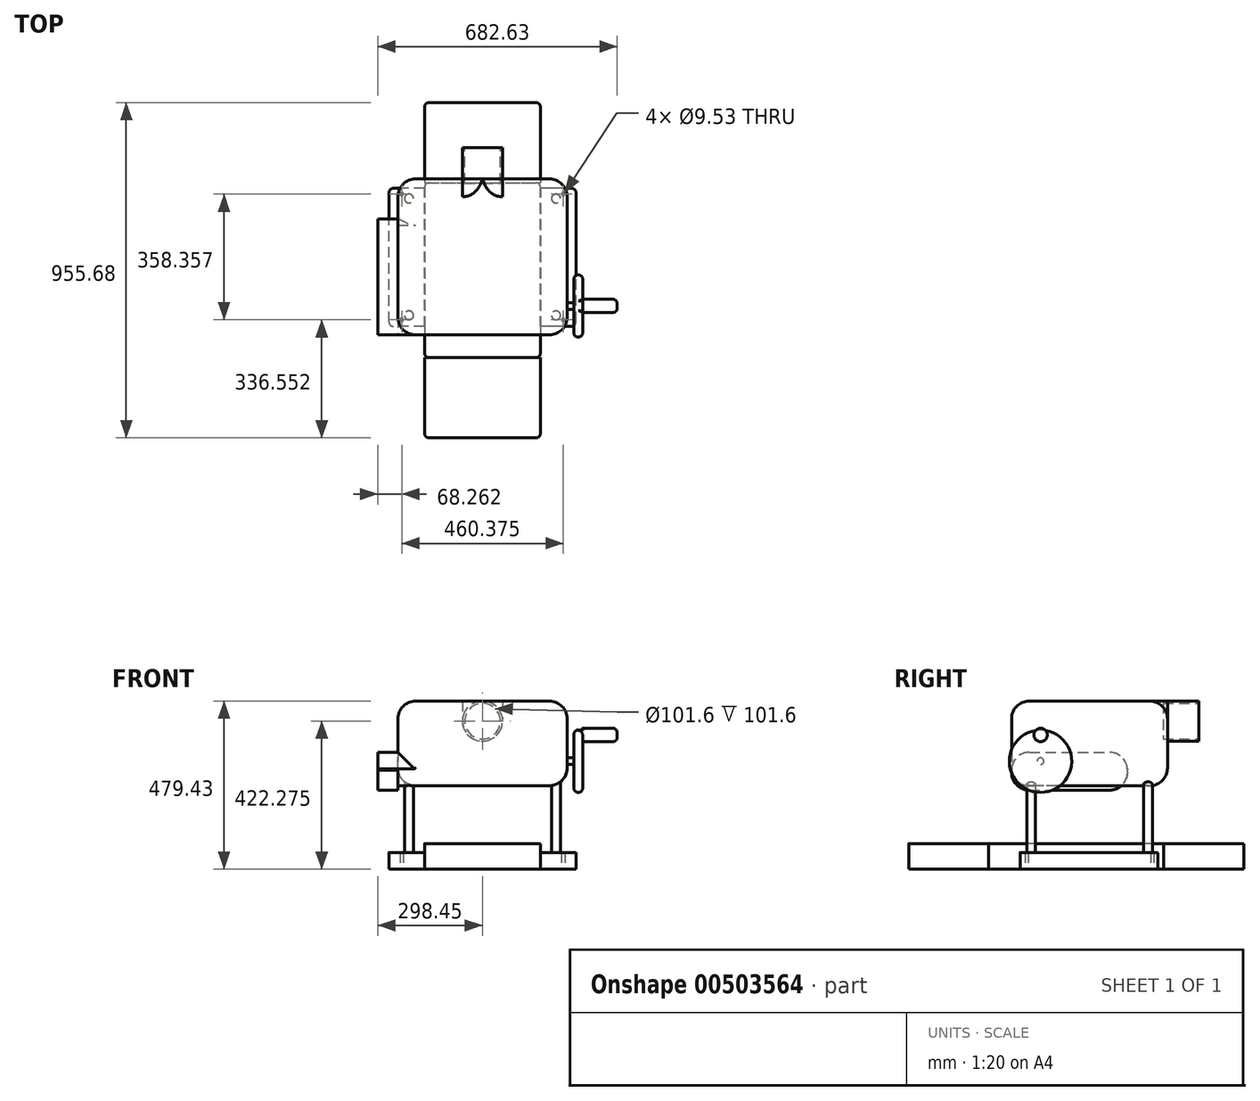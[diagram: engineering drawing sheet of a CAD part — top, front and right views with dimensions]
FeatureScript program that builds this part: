
annotation { "Feature Type Name" : "Feature", "Feature Type Description" : "" }
export const myFeature = defineFeature(function(context is Context, id is Id, definition is map)
    precondition{}
    {
        {
            var Q0;
            Q0=qCreatedBy(makeId("Top.planeOp"),FACE);
            var sketch = newSketch(context, id + "F0", { "sketchPlane" : qUnion([Q0])});
            skLineSegment(sketch, "E0.bottom", {"start": v(266.7, -198.23) * mm, "end": v(-266.7, -198.23) * mm});
            skLineSegment(sketch, "E0.top", {"start": v(266.7, 195.47) * mm, "end": v(-266.7, 195.47) * mm});
            skLineSegment(sketch, "E0.left", {"start": v(266.7, -198.23) * mm, "end": v(266.7, 195.47) * mm});
            skLineSegment(sketch, "E0.right", {"start": v(-266.7, -198.23) * mm, "end": v(-266.7, 195.47) * mm});
            skLineSegment(sketch, "E1", {"start": v(0, 195.47) * mm, "end": v(0, -198.23) * mm, "construction": true});
            skCircle(sketch, "E2", {"center": v(230.19, -179.18) * mm, "radius": 4.76 * mm});
            skCircle(sketch, "E3.MirrorC", {"center": v(-230.19, -179.18) * mm, "radius": 4.76 * mm});
            skCircle(sketch, "E4.MirrorC", {"center": v(230.19, 179.18) * mm, "radius": 4.76 * mm});
            skCircle(sketch, "E5.MirrorC", {"center": v(-230.19, 179.18) * mm, "radius": 4.76 * mm});
            skSolve(sketch);
        }
        {
            var Q0;
            Q0 = qSketchRegion(id + "F0", true);
            extrude(context, id + "F1", {"entities" : qUnion([Q0]), "depth" : 47.62 * mm});
        }
        {
            var Q0;
            Q0=makeQuery(id+"F4.boolean.opBoolean","MERGE",FACE,{"derivedFrom":[makeQuery(id+"F1.opExtrude","SWEPT_FACE",FACE,{"disambiguationData":[OSD([sQuery(id+"F0.wireOp",EDGE,"E0.bottom")])]}),makeQuery(id+"F4.opExtrude","CAP_FACE",FACE,{"disambiguationData":[OSD([sQuery(id+"F3.wireOp",EDGE,"E6.bottom"),sQuery(id+"F3.wireOp",EDGE,"E6.top"),sQuery(id+"F3.wireOp",EDGE,"E6.left"),sQuery(id+"F3.wireOp",EDGE,"E6.right")])],"isStart":true})]});
            cPlane(context, id + "F2", {"entities" : qUnion([Q0]), "cplaneType" : CPlaneType.OFFSET, "offset" : 88.9 * mm, "width" : 152.4 * mm, "height" : 152.4 * mm});
        }
        {
            var Q0;
            Q0=qCreatedBy(id+"F2.planeOp",FACE);
            var sketch = newSketch(context, id + "F3", { "sketchPlane" : qUnion([Q0])});
            skLineSegment(sketch, "E6.bottom", {"start": v(-165.1, 0) * mm, "end": v(165.1, 0) * mm});
            skLineSegment(sketch, "E6.top", {"start": v(-165.1, 73.03) * mm, "end": v(165.1, 73.03) * mm});
            skLineSegment(sketch, "E6.left", {"start": v(-165.1, 0) * mm, "end": v(-165.1, 73.03) * mm});
            skLineSegment(sketch, "E6.right", {"start": v(165.1, 0) * mm, "end": v(165.1, 73.03) * mm});
            skLineSegment(sketch, "E7", {"start": v(0, 73.03) * mm, "end": v(0, 0) * mm, "construction": true});
            skSolve(sketch);
        }
        {
            var Q0;
            Q0 = qSketchRegion(id + "F3", true);
            extrude(context, id + "F4", {"entities" : qUnion([Q0]), "operationType" : NewBodyOperationType.ADD, "oppositeDirection" : true, "depth" : 498.47 * mm});
        }
        {
            var Q0;
            {var subQ0=sQuery(id+"F0.wireOp",EDGE,"E3.MirrorC");var subQ1=sQuery(id+"F0.wireOp",EDGE,"E0.top");var subQ2=sQuery(id+"F0.wireOp",EDGE,"E0.right");var subQ3=sQuery(id+"F0.wireOp",EDGE,"E0.bottom");var subQ4=sQuery(id+"F0.wireOp",EDGE,"E5.MirrorC");Q0=makeQuery(id+"F4.boolean.opBoolean","SPLIT",FACE,{"disambiguationData":[TD([makeQuery(id+"F1.opExtrude","SWEPT_FACE",FACE,{"disambiguationData":[OSD([subQ2])]})])],"derivedFrom":makeQuery(id+"F1.opExtrude","CAP_FACE",FACE,{"disambiguationData":[OSD([subQ3,subQ1,sQuery(id+"F0.wireOp",EDGE,"E0.left"),subQ2,sQuery(id+"F0.wireOp",EDGE,"E2"),subQ0,sQuery(id+"F0.wireOp",EDGE,"E4.MirrorC"),subQ4])],"isStart":false})});}
            var sketch = newSketch(context, id + "F5", { "sketchPlane" : qUnion([Q0])});
            skCircle(sketch, "E8", {"center": v(-209.55, -166.48) * mm, "radius": 12.7 * mm});
            skCircle(sketch, "E9.MirrorC", {"center": v(-209.55, 166.48) * mm, "radius": 12.7 * mm});
            skCircle(sketch, "E10.MirrorC", {"center": v(209.55, 166.48) * mm, "radius": 12.7 * mm});
            skCircle(sketch, "E11.MirrorC", {"center": v(209.55, -166.48) * mm, "radius": 12.7 * mm});
            skSolve(sketch);
        }
        {
            var Q0;
            Q0 = qSketchRegion(id + "F5", true);
            extrude(context, id + "F6", {"entities" : qUnion([Q0]), "operationType" : NewBodyOperationType.ADD, "depth" : 190.5 * mm});
        }
        {
            var Q0;
            Q0=makeQuery(id+"F6.opExtrude","CAP_FACE",FACE,{"disambiguationData":[OSD([sQuery(id+"F5.wireOp",EDGE,"E8")])],"isStart":false});
            var sketch = newSketch(context, id + "F7", { "sketchPlane" : qUnion([Q0])});
            skLineSegment(sketch, "E12.bottom", {"start": v(-241.3, 222.25) * mm, "end": v(241.3, 222.25) * mm});
            skLineSegment(sketch, "E12.top", {"start": v(-241.3, -222.25) * mm, "end": v(241.3, -222.25) * mm});
            skLineSegment(sketch, "E12.left", {"start": v(-241.3, 222.25) * mm, "end": v(-241.3, -222.25) * mm});
            skLineSegment(sketch, "E12.right", {"start": v(241.3, 222.25) * mm, "end": v(241.3, -222.25) * mm});
            skPoint(sketch, "E12.middle", {"position": v(0, 0) * mm});
            skSolve(sketch);
        }
        {
            var Q0;
            Q0 = qSketchRegion(id + "F7", true);
            extrude(context, id + "F8", {"entities" : qUnion([Q0]), "operationType" : NewBodyOperationType.ADD, "depth" : 241.3 * mm});
        }
        {
            var Q0;
            Q0=makeQuery(id+"F8.opExtrude","SWEPT_FACE",FACE,{"disambiguationData":[OSD([sQuery(id+"F7.wireOp",EDGE,"E12.right")])]});
            var sketch = newSketch(context, id + "F9", { "sketchPlane" : qUnion([Q0])});
            skCircle(sketch, "E13", {"center": v(-139.7, 307.98) * mm, "radius": 9.52 * mm});
            skSolve(sketch);
        }
        {
            var Q0;
            Q0 = qSketchRegion(id + "F9", true);
            extrude(context, id + "F10", {"entities" : qUnion([Q0]), "operationType" : NewBodyOperationType.ADD, "depth" : 19.05 * mm});
        }
        {
            var Q0;
            Q0=makeQuery(id+"F10.opExtrude","CAP_FACE",FACE,{"disambiguationData":[OSD([sQuery(id+"F9.wireOp",EDGE,"E13")])],"isStart":false});
            var sketch = newSketch(context, id + "F11", { "sketchPlane" : qUnion([Q0])});
            skCircle(sketch, "E14", {"center": v(-139.7, 307.98) * mm, "radius": 88.9 * mm});
            skSolve(sketch);
        }
        {
            var Q0;
            Q0 = qSketchRegion(id + "F11", true);
            extrude(context, id + "F12", {"entities" : qUnion([Q0]), "operationType" : NewBodyOperationType.ADD, "depth" : 25.4 * mm});
        }
        {
            var Q0;
            Q0=makeQuery(id+"F12.opExtrude","CAP_FACE",FACE,{"disambiguationData":[OSD([sQuery(id+"F11.wireOp",EDGE,"E14")])],"isStart":false});
            var sketch = newSketch(context, id + "F13", { "sketchPlane" : qUnion([Q0])});
            skCircle(sketch, "E15", {"center": v(-139.45, 382.88) * mm, "radius": 19.05 * mm});
            skSolve(sketch);
        }
        {
            var Q0;
            Q0 = qSketchRegion(id + "F13", true);
            extrude(context, id + "F14", {"entities" : qUnion([Q0]), "operationType" : NewBodyOperationType.ADD, "depth" : 98.42 * mm});
        }
        {
            var Q0;
            Q0=makeQuery(id+"F4.opExtrude","CAP_FACE",FACE,{"disambiguationData":[OSD([sQuery(id+"F3.wireOp",EDGE,"E6.bottom"),sQuery(id+"F3.wireOp",EDGE,"E6.top"),sQuery(id+"F3.wireOp",EDGE,"E6.left"),sQuery(id+"F3.wireOp",EDGE,"E6.right")])],"isStart":true});
            var sketch = newSketch(context, id + "F15", { "sketchPlane" : qUnion([Q0])});
            skLineSegment(sketch, "E16.0.0", {"start": v(165.1, 73.03) * mm, "end": v(-165.1, 73.03) * mm});
            skLineSegment(sketch, "E16.0.1", {"start": v(-165.1, 73.03) * mm, "end": v(-165.1, 0) * mm});
            skLineSegment(sketch, "E16.0.2", {"start": v(-165.1, 0) * mm, "end": v(165.1, 0) * mm});
            skLineSegment(sketch, "E16.0.3", {"start": v(165.1, 0) * mm, "end": v(165.1, 73.03) * mm});
            skSolve(sketch);
        }
        {
            var Q0;
            Q0 = qSketchRegion(id + "F15", true);
            extrude(context, id + "F16", {"entities" : qUnion([Q0]), "depth" : 228.6 * mm});
        }
        {
            var Q0;
            Q0=makeQuery(id+"F4.opExtrude","CAP_FACE",FACE,{"disambiguationData":[OSD([sQuery(id+"F3.wireOp",EDGE,"E6.bottom"),sQuery(id+"F3.wireOp",EDGE,"E6.top"),sQuery(id+"F3.wireOp",EDGE,"E6.left"),sQuery(id+"F3.wireOp",EDGE,"E6.right")])],"isStart":false});
            var sketch = newSketch(context, id + "F17", { "sketchPlane" : qUnion([Q0])});
            skLineSegment(sketch, "E17.0.0", {"start": v(165.1, 73.03) * mm, "end": v(-165.1, 73.03) * mm});
            skLineSegment(sketch, "E17.0.1", {"start": v(-165.1, 73.03) * mm, "end": v(-165.1, 0) * mm});
            skLineSegment(sketch, "E17.0.2", {"start": v(-165.1, 0) * mm, "end": v(165.1, 0) * mm});
            skLineSegment(sketch, "E17.0.3", {"start": v(165.1, 0) * mm, "end": v(165.1, 73.03) * mm});
            skSolve(sketch);
        }
        {
            var Q0;
            Q0 = qSketchRegion(id + "F17", true);
            extrude(context, id + "F18", {"entities" : qUnion([Q0]), "depth" : 228.6 * mm});
        }
        {
            var Q0;
            Q0=makeQuery(id+"F8.opExtrude","SWEPT_FACE",FACE,{"disambiguationData":[OSD([sQuery(id+"F7.wireOp",EDGE,"E12.left")])]});
            var sketch = newSketch(context, id + "F19", { "sketchPlane" : qUnion([Q0])});
            skLineSegment(sketch, "E18.bottom", {"start": v(222.25, 225.43) * mm, "end": v(-107.95, 225.43) * mm});
            skLineSegment(sketch, "E18.top", {"start": v(222.25, 333.38) * mm, "end": v(-107.95, 333.38) * mm});
            skLineSegment(sketch, "E18.left", {"start": v(222.25, 225.43) * mm, "end": v(222.25, 333.38) * mm});
            skLineSegment(sketch, "E18.right", {"start": v(-107.95, 225.43) * mm, "end": v(-107.95, 333.38) * mm});
            skPoint(sketch, "E18.middle", {"position": v(57.15, 279.4) * mm});
            skSolve(sketch);
        }
        {
            var Q0;
            Q0 = qSketchRegion(id + "F19", true);
            extrude(context, id + "F20", {"entities" : qUnion([Q0]), "operationType" : NewBodyOperationType.ADD, "depth" : 57.15 * mm});
        }
        {
            var Q0;
            Q0=makeQuery(id+"F8.opExtrude","SWEPT_FACE",FACE,{"disambiguationData":[OSD([sQuery(id+"F7.wireOp",EDGE,"E12.bottom")])]});
            var sketch = newSketch(context, id + "F21", { "sketchPlane" : qUnion([Q0])});
            skCircle(sketch, "E19", {"center": v(0, 422.28) * mm, "radius": 57.15 * mm});
            skSolve(sketch);
        }
        {
            var Q0;
            Q0 = qSketchRegion(id + "F21", true);
            extrude(context, id + "F22", {"entities" : qUnion([Q0]), "operationType" : NewBodyOperationType.ADD, "depth" : 88.9 * mm});
        }
        {
            var Q0;
            Q0=makeQuery(id+"F8.opExtrude","SWEPT_EDGE",EDGE,{"disambiguationData":[OSD([sQuery(id+"F7.wireOp",EDGE,"E12.top"),sQuery(id+"F7.wireOp",EDGE,"E12.right")])]});
            var Q1;
            Q1=makeQuery(id+"F8.opExtrude","SWEPT_EDGE",EDGE,{"disambiguationData":[OSD([sQuery(id+"F7.wireOp",EDGE,"E12.top"),sQuery(id+"F7.wireOp",EDGE,"E12.left")])]});
            var Q2;
            Q2=makeQuery(id+"F8.opExtrude","SWEPT_EDGE",EDGE,{"disambiguationData":[OSD([sQuery(id+"F7.wireOp",EDGE,"E12.bottom"),sQuery(id+"F7.wireOp",EDGE,"E12.right")])]});
            var Q3;
            Q3=makeQuery(id+"F8.opExtrude","SWEPT_EDGE",EDGE,{"disambiguationData":[OSD([sQuery(id+"F7.wireOp",EDGE,"E12.bottom"),sQuery(id+"F7.wireOp",EDGE,"E12.left")])]});
            var Q4;
            Q4=makeQuery(id+"F8.opExtrude","CAP_FACE",FACE,{"disambiguationData":[OSD([sQuery(id+"F7.wireOp",EDGE,"E12.bottom"),sQuery(id+"F7.wireOp",EDGE,"E12.top"),sQuery(id+"F7.wireOp",EDGE,"E12.left"),sQuery(id+"F7.wireOp",EDGE,"E12.right")])],"isStart":false});
            fillet(context, id + "F23", {"entities" : qUnion([Q0, Q1, Q2, Q3, Q4]), "radius" : 50.8 * mm, "tangentPropagation" : true, "allowEdgeOverflow" : false});
        }
        {
            var Q0;
            Q0=makeQuery(id+"F1.opExtrude","SWEPT_EDGE",EDGE,{"disambiguationData":[OSD([sQuery(id+"F0.wireOp",EDGE,"E0.top"),sQuery(id+"F0.wireOp",EDGE,"E0.left")])]});
            var Q1;
            Q1=makeQuery(id+"F1.opExtrude","SWEPT_EDGE",EDGE,{"disambiguationData":[OSD([sQuery(id+"F0.wireOp",EDGE,"E0.bottom"),sQuery(id+"F0.wireOp",EDGE,"E0.left")])]});
            var Q2;
            Q2=makeQuery(id+"F4.opExtrude","CAP_EDGE",EDGE,{"disambiguationData":[OSD([sQuery(id+"F3.wireOp",EDGE,"E6.right")])],"isStart":true});
            var Q3;
            Q3=makeQuery(id+"F4.opExtrude","CAP_EDGE",EDGE,{"disambiguationData":[OSD([sQuery(id+"F3.wireOp",EDGE,"E6.right")])],"isStart":false});
            var Q4;
            Q4=makeQuery(id+"F1.opExtrude","SWEPT_EDGE",EDGE,{"disambiguationData":[OSD([sQuery(id+"F0.wireOp",EDGE,"E0.top"),sQuery(id+"F0.wireOp",EDGE,"E0.right")])]});
            var Q5;
            Q5=makeQuery(id+"F1.opExtrude","SWEPT_EDGE",EDGE,{"disambiguationData":[OSD([sQuery(id+"F0.wireOp",EDGE,"E0.bottom"),sQuery(id+"F0.wireOp",EDGE,"E0.right")])]});
            var Q6;
            Q6=makeQuery(id+"F4.opExtrude","CAP_EDGE",EDGE,{"disambiguationData":[OSD([sQuery(id+"F3.wireOp",EDGE,"E6.left")])],"isStart":true});
            var Q7;
            Q7=makeQuery(id+"F4.opExtrude","CAP_EDGE",EDGE,{"disambiguationData":[OSD([sQuery(id+"F3.wireOp",EDGE,"E6.left")])],"isStart":false});
            var Q8;
            Q8=makeQuery(id+"F18.opExtrude","CAP_EDGE",EDGE,{"disambiguationData":[OSD([sQuery(id+"F17.wireOp",EDGE,"E17.0.3")])],"isStart":false});
            var Q9;
            Q9=makeQuery(id+"F18.opExtrude","CAP_EDGE",EDGE,{"disambiguationData":[OSD([sQuery(id+"F17.wireOp",EDGE,"E17.0.1")])],"isStart":false});
            var Q10;
            Q10=makeQuery(id+"F16.opExtrude","CAP_EDGE",EDGE,{"disambiguationData":[OSD([sQuery(id+"F15.wireOp",EDGE,"E16.0.1")])],"isStart":false});
            var Q11;
            Q11=makeQuery(id+"F16.opExtrude","CAP_EDGE",EDGE,{"disambiguationData":[OSD([sQuery(id+"F15.wireOp",EDGE,"E16.0.3")])],"isStart":false});
            var Q12;
            {var subQ0=sQuery(id+"F11.wireOp",EDGE,"E14");Q12=makeQuery(id+"F14.boolean.opBoolean","SPLIT",EDGE,{"disambiguationData":[topologyDisambiguationEdgeConnected([makeQuery(id+"F12.opExtrude","CAP_FACE",FACE,{"disambiguationData":[OSD([subQ0])],"isStart":false})])],"derivedFrom":makeQuery(id+"F12.opExtrude","CAP_EDGE",EDGE,{"disambiguationData":[OSD([subQ0])],"isStart":false})});}
            var Q13;
            Q13=makeQuery(id+"F12.opExtrude","CAP_EDGE",EDGE,{"disambiguationData":[OSD([sQuery(id+"F11.wireOp",EDGE,"E14")])],"isStart":true});
            var Q14;
            Q14=makeQuery(id+"F14.opExtrude","CAP_EDGE",EDGE,{"disambiguationData":[OSD([sQuery(id+"F13.wireOp",EDGE,"E15")])],"isStart":false});
            fillet(context, id + "F24", {"entities" : qUnion([Q0, Q1, Q2, Q3, Q4, Q5, Q6, Q7, Q8, Q9, Q10, Q11, Q12, Q13, Q14]), "radius" : 12.7 * mm, "tangentPropagation" : true, "allowEdgeOverflow" : false});
        }
        {
            var Q0;
            Q0=makeQuery(id+"F22.opExtrude","CAP_FACE",FACE,{"disambiguationData":[OSD([sQuery(id+"F21.wireOp",EDGE,"E19")])],"isStart":false});
            var sketch = newSketch(context, id + "F25", { "sketchPlane" : qUnion([Q0])});
            skCircle(sketch, "E20.0", {"center": v(0, 422.28) * mm, "radius": 50.8 * mm});
            skSolve(sketch);
        }
        {
            var Q0;
            Q0 = qSketchRegion(id + "F25", true);
            extrude(context, id + "F26", {"entities" : qUnion([Q0]), "operationType" : NewBodyOperationType.REMOVE, "oppositeDirection" : true, "depth" : 101.6 * mm});
        }
        {
            var Q0;
            Q0=makeQuery(id+"F20.opExtrude","SWEPT_EDGE",EDGE,{"disambiguationData":[OSD([sQuery(id+"F19.wireOp",EDGE,"E18.top"),sQuery(id+"F19.wireOp",EDGE,"E18.right")])]});
            var Q1;
            Q1=makeQuery(id+"F20.opExtrude","SWEPT_EDGE",EDGE,{"disambiguationData":[OSD([sQuery(id+"F19.wireOp",EDGE,"E18.bottom"),sQuery(id+"F19.wireOp",EDGE,"E18.right")])]});
            var Q2;
            Q2=makeQuery(id+"F20.opExtrude","SWEPT_EDGE",EDGE,{"disambiguationData":[OSD([sQuery(id+"F19.wireOp",EDGE,"E18.bottom"),sQuery(id+"F19.wireOp",EDGE,"E18.left")])]});
            var Q3;
            Q3=makeQuery(id+"F20.opExtrude","SWEPT_EDGE",EDGE,{"disambiguationData":[OSD([sQuery(id+"F7.wireOp",EDGE,"E12.top"),sQuery(id+"F7.wireOp",EDGE,"E12.left"),sQuery(id+"F19.wireOp",EDGE,"E18.top"),sQuery(id+"F19.wireOp",EDGE,"E18.left")])]});
            fillet(context, id + "F27", {"entities" : qUnion([Q0, Q1, Q2, Q3]), "radius" : 50.8 * mm, "tangentPropagation" : true, "allowEdgeOverflow" : false});
        }
        {
            var Q0;
            Q0=makeQuery(id+"F8.opExtrude","CAP_EDGE",EDGE,{"disambiguationData":[OSD([sQuery(id+"F7.wireOp",EDGE,"E12.bottom")])],"isStart":true});
            fillet(context, id + "F28", {"entities" : qUnion([Q0]), "radius" : 50.8 * mm, "tangentPropagation" : true, "allowEdgeOverflow" : false});
        }
    });
